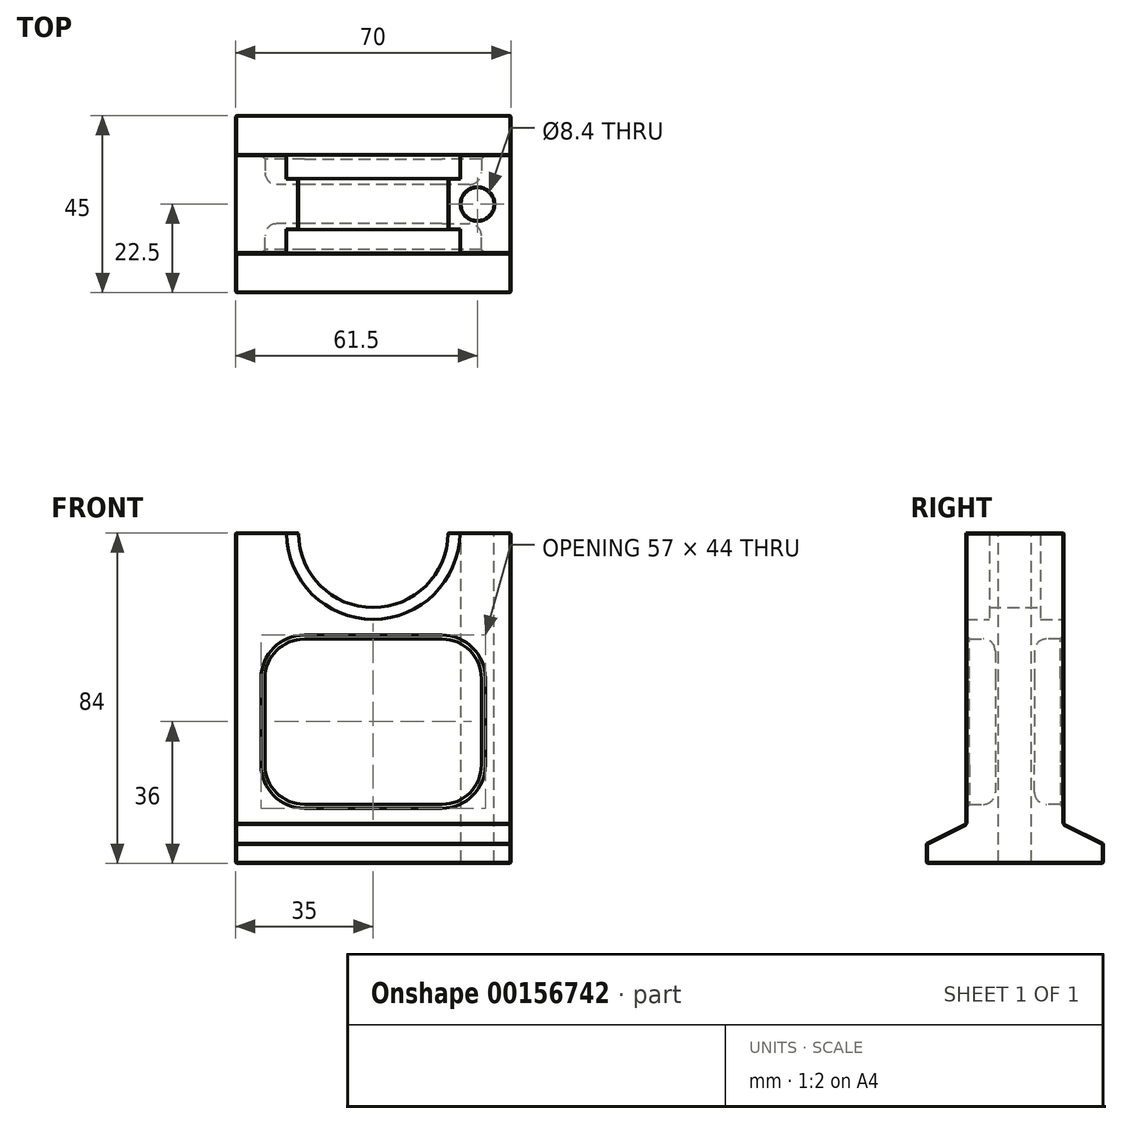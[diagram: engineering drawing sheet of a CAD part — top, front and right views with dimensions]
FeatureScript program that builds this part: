
annotation { "Feature Type Name" : "Feature", "Feature Type Description" : "" }
export const myFeature = defineFeature(function(context is Context, id is Id, definition is map)
    precondition{}
    {
        {
            var Q0;
            Q0=qCreatedBy(makeId("Front.planeOp"),FACE);
            var sketch = newSketch(context, id + "F0", { "sketchPlane" : qUnion([Q0])});
            skLineSegment(sketch, "E0.bottom", {"start": v(35, 37) * mm, "end": v(19, 37) * mm});
            skLineSegment(sketch, "E0.top", {"start": v(35, -37) * mm, "end": v(-35, -37) * mm});
            skLineSegment(sketch, "E0.left", {"start": v(35, 37) * mm, "end": v(35, -37) * mm});
            skLineSegment(sketch, "E0.right", {"start": v(-35, 37) * mm, "end": v(-35, -37) * mm});
            skPoint(sketch, "E0.middle", {"position": v(0, 0) * mm});
            skLineSegment(sketch, "E1", {"start": v(-19, 37) * mm, "end": v(-35, 37) * mm});
            skArc(sketch, "E2", {"start": v(-19, 37) * mm, "mid": v(0, 18) * mm, "end": v(19, 37) * mm});
            skArc(sketch, "E3", {"start": v(-22, 37) * mm, "mid": v(0, 15) * mm, "end": v(22, 37) * mm});
            skLineSegment(sketch, "E4", {"start": v(0, 15) * mm, "end": v(0, -37) * mm, "construction": true});
            skLineSegment(sketch, "E5.bottom", {"start": v(17.5, 10) * mm, "end": v(-17.5, 10) * mm});
            skLineSegment(sketch, "E5.top", {"start": v(17.5, -32) * mm, "end": v(-17.5, -32) * mm});
            skLineSegment(sketch, "E5.left", {"start": v(27.5, 0) * mm, "end": v(27.5, -22) * mm});
            skLineSegment(sketch, "E5.right", {"start": v(-27.5, 0) * mm, "end": v(-27.5, -22) * mm});
            skPoint(sketch, "E5.middle", {"position": v(0, -11) * mm});
            skPoint(sketch, "E6.visualSharp", {"position": v(-27.5, 10) * mm});
            skArc(sketch, "E6.filletArc", {"start": v(-17.5, 10) * mm, "mid": v(-24.57, 7.07) * mm, "end": v(-27.5, 0) * mm});
            skPoint(sketch, "E7.visualSharp", {"position": v(27.5, 10) * mm});
            skArc(sketch, "E7.filletArc", {"start": v(27.5, 0) * mm, "mid": v(24.57, 7.07) * mm, "end": v(17.5, 10) * mm});
            skPoint(sketch, "E8.visualSharp", {"position": v(27.5, -32) * mm});
            skArc(sketch, "E8.filletArc", {"start": v(17.5, -32) * mm, "mid": v(24.57, -29.07) * mm, "end": v(27.5, -22) * mm});
            skPoint(sketch, "E9.visualSharp", {"position": v(-27.5, -32) * mm});
            skArc(sketch, "E9.filletArc", {"start": v(-27.5, -22) * mm, "mid": v(-24.57, -29.07) * mm, "end": v(-17.5, -32) * mm});
            skSolve(sketch);
        }
        {
            var Q0;
            Q0=makeQuery(id+"F0.imprint","IMPRINT",FACE,{"disambiguationData":[TD([[makeQuery(id+"F0.imprint","IMPRINT",EDGE,{"derivedFrom":sQuery(id+"F0.wireOp",EDGE,"E0.top")}),-1.0]])]});
            var Q1;
            Q1=makeQuery(id+"F0.imprint","IMPRINT",FACE,{"disambiguationData":[TD([[makeQuery(id+"F0.imprint","IMPRINT",EDGE,{"derivedFrom":sQuery(id+"F0.wireOp",EDGE,"E5.bottom")}),1.0]])]});
            extrude(context, id + "F1", {"entities" : qUnion([Q0, Q1]), "endBound" : BoundingType.SYMMETRIC, "depth" : 25 * mm});
        }
        {
            var Q0;
            {var subQ0=sQuery(id+"F0.wireOp",EDGE,"E2");Q0=makeQuery(id+"F0.imprint","IMPRINT",FACE,{"disambiguationData":[TD([[makeQuery(id+"F0.imprint","IMPRINT",EDGE,{"derivedFrom":subQ0}),-1.0]])]});}
            extrude(context, id + "F2", {"entities" : qUnion([Q0]), "operationType" : NewBodyOperationType.ADD, "endBound" : BoundingType.SYMMETRIC, "depth" : 13 * mm});
        }
        {
            var Q0;
            Q0=makeQuery(id+"F1.opExtrude","SWEPT_FACE",FACE,{"disambiguationData":[OSD([sQuery(id+"F0.wireOp",EDGE,"E0.top")])]});
            var sketch = newSketch(context, id + "F3", { "sketchPlane" : qUnion([Q0])});
            skLineSegment(sketch, "E10.bottom", {"start": v(35, 22.5) * mm, "end": v(-35, 22.5) * mm});
            skLineSegment(sketch, "E10.top", {"start": v(35, -22.5) * mm, "end": v(-35, -22.5) * mm});
            skLineSegment(sketch, "E10.left", {"start": v(35, 22.5) * mm, "end": v(35, -22.5) * mm});
            skLineSegment(sketch, "E10.right", {"start": v(-35, 22.5) * mm, "end": v(-35, -22.5) * mm});
            skPoint(sketch, "E10.middle", {"position": v(0, 0) * mm});
            skPoint(sketch, "E10.cornerSnap0", {"position": v(35, 0) * mm});
            skSolve(sketch);
        }
        {
            var Q0;
            {var subQ0=sQuery(id+"F3.wireOp",EDGE,"E10.bottom");Q0=makeQuery(id+"F3.imprint","IMPRINT",FACE,{"disambiguationData":[TD([[makeQuery(id+"F3.imprint","IMPRINT",EDGE,{"derivedFrom":subQ0}),1.0]])]});}
            var Q1;
            {var subQ1=sQuery(id+"F0.wireOp",EDGE,"E0.top");var subQ2=makeQuery(id+"F1.opExtrude","CAP_EDGE",EDGE,{"disambiguationData":[OSD([subQ1])],"isStart":true});Q1=makeQuery(id+"F3.imprint","IMPRINT",FACE,{"disambiguationData":[TD([[makeQuery(id+"F3.imprint","IMPRINT",EDGE,{"derivedFrom":subQ2}),-1.0]])]});}
            var Q2;
            {var subQ0=sQuery(id+"F3.wireOp",EDGE,"E10.top");Q2=makeQuery(id+"F3.imprint","IMPRINT",FACE,{"disambiguationData":[TD([[makeQuery(id+"F3.imprint","IMPRINT",EDGE,{"derivedFrom":subQ0}),-1.0]])]});}
            extrude(context, id + "F4", {"entities" : qUnion([Q0, Q1, Q2]), "operationType" : NewBodyOperationType.ADD, "depth" : 10 * mm});
        }
        {
            var Q0;
            Q0=makeQuery(id+"F4.opExtrude","CAP_EDGE",EDGE,{"disambiguationData":[OSD([sQuery(id+"F3.wireOp",EDGE,"E10.bottom")])],"isStart":true});
            chamfer(context, id + "F5", {"entities" : qUnion([Q0]), "chamferType" : ChamferType.TWO_OFFSETS, "width1" : 5 * mm, "oppositeDirection" : false, "width2" : 10 * mm, "tangentPropagation" : true});
        }
        {
            var Q0;
            Q0=makeQuery(id+"F4.opExtrude","CAP_EDGE",EDGE,{"disambiguationData":[OSD([sQuery(id+"F3.wireOp",EDGE,"E10.top")])],"isStart":true});
            chamfer(context, id + "F6", {"entities" : qUnion([Q0]), "chamferType" : ChamferType.TWO_OFFSETS, "width1" : 10 * mm, "oppositeDirection" : false, "width2" : 5 * mm, "tangentPropagation" : true});
        }
        {
            var Q0;
            {var subQ0=sQuery(id+"F0.wireOp",EDGE,"E0.bottom");Q0=makeQuery(id+"F2.boolean.opBoolean","MERGE",FACE,{"derivedFrom":[makeQuery(id+"F1.opExtrude","SWEPT_FACE",FACE,{"disambiguationData":[OSD([subQ0])]}),makeQuery(id+"F2.opExtrude","SWEPT_FACE",FACE,{"disambiguationData":[OSD([subQ0])]})]});}
            var sketch = newSketch(context, id + "F7", { "sketchPlane" : qUnion([Q0])});
            skLineSegment(sketch, "E11", {"start": v(26.5, 0) * mm, "end": v(-26.5, 0) * mm, "construction": true});
            skPoint(sketch, "E11.endSnap0", {"position": v(19, 0) * mm});
            skCircle(sketch, "E12", {"center": v(26.5, 0) * mm, "radius": 4.2 * mm});
            skCircle(sketch, "E13.MirrorC", {"center": v(-26.5, 0) * mm, "radius": 4.2 * mm});
            skSolve(sketch);
        }
        {
            var Q0;
            Q0=makeQuery(id+"F7.imprint","IMPRINT",FACE,{"disambiguationData":[TD([[makeQuery(id+"F7.imprint","IMPRINT",EDGE,{"derivedFrom":sQuery(id+"F7.wireOp",EDGE,"E12")}),1.0]])]});
            var Q1;
            Q1=makeQuery(id+"F7.imprint","IMPRINT",FACE,{"disambiguationData":[TD([[makeQuery(id+"F7.imprint","IMPRINT",EDGE,{"derivedFrom":sQuery(id+"F7.wireOp",EDGE,"E13.MirrorC")}),-1.0]])]});
            extrude(context, id + "F8", {"entities" : qUnion([Q0, Q1]), "operationType" : NewBodyOperationType.REMOVE, "endBound" : BoundingType.THROUGH_ALL, "oppositeDirection" : true, "depth" : 25 * mm});
        }
        {
            var Q0;
            {var subQ0=sQuery(id+"F0.wireOp",EDGE,"E0.bottom");Q0=makeQuery(id+"F2.boolean.opBoolean","MERGE",FACE,{"derivedFrom":[makeQuery(id+"F1.opExtrude","SWEPT_FACE",FACE,{"disambiguationData":[OSD([subQ0])]}),makeQuery(id+"F2.opExtrude","SWEPT_FACE",FACE,{"disambiguationData":[OSD([subQ0])]})]});}
            var Q1;
            {var subQ0=sQuery(id+"F0.wireOp",EDGE,"E1");Q1=makeQuery(id+"F2.boolean.opBoolean","MERGE",FACE,{"derivedFrom":[makeQuery(id+"F1.opExtrude","SWEPT_FACE",FACE,{"disambiguationData":[OSD([subQ0])]}),makeQuery(id+"F2.opExtrude","SWEPT_FACE",FACE,{"disambiguationData":[OSD([subQ0])]})]});}
            chamfer(context, id + "F9", {"entities" : qUnion([Q0, Q1]), "width" : .2 * mm, "tangentPropagation" : true});
        }
        {
            var Q0;
            Q0=makeQuery(id+"F4.boolean.opBoolean","MERGE",FACE,{"derivedFrom":[makeQuery(id+"F1.opExtrude","SWEPT_FACE",FACE,{"disambiguationData":[OSD([sQuery(id+"F0.wireOp",EDGE,"E0.left")])]}),makeQuery(id+"F4.opExtrude","SWEPT_FACE",FACE,{"disambiguationData":[OSD([sQuery(id+"F3.wireOp",EDGE,"E10.left")])]})]});
            var Q1;
            Q1=makeQuery(id+"F4.boolean.opBoolean","MERGE",FACE,{"derivedFrom":[makeQuery(id+"F1.opExtrude","SWEPT_FACE",FACE,{"disambiguationData":[OSD([sQuery(id+"F0.wireOp",EDGE,"E0.right")])]}),makeQuery(id+"F4.opExtrude","SWEPT_FACE",FACE,{"disambiguationData":[OSD([sQuery(id+"F3.wireOp",EDGE,"E10.right")])]})]});
            var Q2;
            Q2=makeQuery(id+"F4.opExtrude","CAP_FACE",FACE,{"disambiguationData":[OSD([sQuery(id+"F3.wireOp",EDGE,"E10.bottom"),sQuery(id+"F3.wireOp",EDGE,"E10.top"),sQuery(id+"F3.wireOp",EDGE,"E10.left"),sQuery(id+"F3.wireOp",EDGE,"E10.right")])],"isStart":false});
            var Q3;
            Q3=makeQuery(id+"F6.opChamfer","BLEND_FACE",FACE,{"disambiguationData":[OSD([sQuery(id+"F3.wireOp",EDGE,"E10.top")])]});
            var Q4;
            Q4=makeQuery(id+"F5.opChamfer","BLEND_FACE",FACE,{"disambiguationData":[OSD([sQuery(id+"F3.wireOp",EDGE,"E10.bottom")])]});
            chamfer(context, id + "F10", {"entities" : qUnion([Q0, Q1, Q2, Q3, Q4]), "width" : .25 * mm, "tangentPropagation" : true});
        }
        {
            var Q0;
            Q0=makeQuery(id+"F0.imprint","IMPRINT",FACE,{"disambiguationData":[TD([[makeQuery(id+"F0.imprint","IMPRINT",EDGE,{"derivedFrom":sQuery(id+"F0.wireOp",EDGE,"E5.bottom")}),1.0]])]});
            extrude(context, id + "F11", {"entities" : qUnion([Q0]), "operationType" : NewBodyOperationType.REMOVE, "depth" : 20 * mm, "hasSecondDirection" : true, "secondDirectionOppositeDirection" : false, "secondDirectionDepth" : 5 * mm});
        }
        {
            var Q0;
            Q0=makeQuery(id+"F0.imprint","IMPRINT",FACE,{"disambiguationData":[TD([[makeQuery(id+"F0.imprint","IMPRINT",EDGE,{"derivedFrom":sQuery(id+"F0.wireOp",EDGE,"E5.bottom")}),1.0]])]});
            extrude(context, id + "F12", {"entities" : qUnion([Q0]), "operationType" : NewBodyOperationType.REMOVE, "oppositeDirection" : true, "depth" : 25 * mm, "hasSecondDirection" : true, "secondDirectionOppositeDirection" : true, "secondDirectionDepth" : 5 * mm});
        }
        {
            var Q0;
            Q0=makeQuery(id+"F11.boolean.opBoolean","COPY",EDGE,{"derivedFrom":makeQuery(id+"F11.opExtrude","CAP_EDGE",EDGE,{"disambiguationData":[OSD([sQuery(id+"F0.wireOp",EDGE,"E5.right")])],"isStart":true})});
            var Q1;
            Q1=makeQuery(id+"F12.boolean.opBoolean","COPY",EDGE,{"derivedFrom":makeQuery(id+"F12.opExtrude","CAP_EDGE",EDGE,{"disambiguationData":[OSD([sQuery(id+"F0.wireOp",EDGE,"E5.right")])],"isStart":true})});
            fillet(context, id + "F13", {"entities" : qUnion([Q0, Q1]), "radius" : 3 * mm, "tangentPropagation" : true, "allowEdgeOverflow" : false});
        }
        {
            var Q0;
            Q0=makeQuery(id+"F11.boolean.opBoolean","INTERSECT",EDGE,{"derivedFrom":[makeQuery(id+"F1.opExtrude","CAP_FACE",FACE,{"disambiguationData":[OSD([sQuery(id+"F0.wireOp",EDGE,"E0.bottom"),sQuery(id+"F0.wireOp",EDGE,"E0.top"),sQuery(id+"F0.wireOp",EDGE,"E0.left"),sQuery(id+"F0.wireOp",EDGE,"E0.right"),sQuery(id+"F0.wireOp",EDGE,"E1"),sQuery(id+"F0.wireOp",EDGE,"E3")])],"isStart":false}),makeQuery(id+"F11.opExtrude","SWEPT_FACE",FACE,{"disambiguationData":[OSD([sQuery(id+"F0.wireOp",EDGE,"E5.right")])]})]});
            var Q1;
            Q1=makeQuery(id+"F12.boolean.opBoolean","INTERSECT",EDGE,{"derivedFrom":[makeQuery(id+"F1.opExtrude","CAP_FACE",FACE,{"disambiguationData":[OSD([sQuery(id+"F0.wireOp",EDGE,"E0.bottom"),sQuery(id+"F0.wireOp",EDGE,"E0.top"),sQuery(id+"F0.wireOp",EDGE,"E0.left"),sQuery(id+"F0.wireOp",EDGE,"E0.right"),sQuery(id+"F0.wireOp",EDGE,"E1"),sQuery(id+"F0.wireOp",EDGE,"E3")])],"isStart":true}),makeQuery(id+"F12.opExtrude","SWEPT_FACE",FACE,{"disambiguationData":[OSD([sQuery(id+"F0.wireOp",EDGE,"E5.right")])]})]});
            chamfer(context, id + "F14", {"entities" : qUnion([Q0, Q1]), "width" : 1 * mm, "tangentPropagation" : true});
        }
    });
